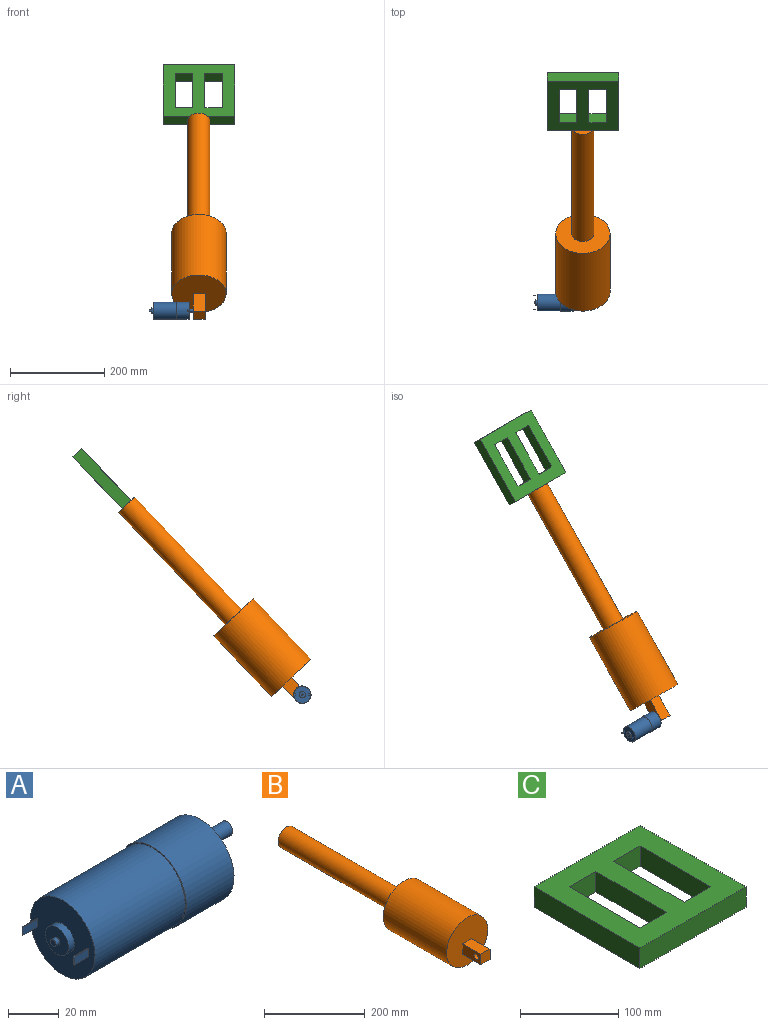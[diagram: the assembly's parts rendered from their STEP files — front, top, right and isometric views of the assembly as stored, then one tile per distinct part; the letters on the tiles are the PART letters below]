
ASSEMBLY  parts=3 mates=5
PART A: 70 faces, bbox 106.2x37x37 mm
  f0: torus R=1.65mm, axis (1,0,0), area 2.2mm2, adj f5,f45
  f1: torus R=1.65mm, axis (1,0,0), area 2.2mm2, adj f3,f47
  f2: torus R=1.65mm, axis (1,0,0), area 2.2mm2, adj f4,f46
  f3: cylinder r=1.78mm len=3.56mm, axis (-1,0,0), area 24.1mm2, adj f1,f19
  f4: cylinder r=1.78mm len=3.56mm, axis (-1,0,0), area 24.1mm2, adj f2,f20
  f5: cylinder r=1.78mm len=3.56mm, axis (-1,0,0), area 24.1mm2, adj f0,f21
  f6: cylinder r=1.91mm len=3.81mm, axis (1,0,0), area 30.4mm2, adj f20,f25
  f7: cylinder r=1.91mm len=3.81mm, axis (1,0,0), area 30.4mm2, adj f21,f25
  f8: cylinder r=1.91mm len=3.81mm, axis (1,0,0), area 30.4mm2, adj f19,f25
  f9: cylinder r=1.57mm len=3.15mm, axis (1,0,0), area 21.1mm2, adj f23,f32
  f10: cylinder r=6.45mm len=12.9mm, axis (1,0,0), area 128.7mm2, adj f22,f23
  f11: cylinder r=1.73mm len=3.5mm, axis (1,0,0), area 38mm2, adj f25,f31
  f12: cylinder r=1.73mm len=3.5mm, axis (1,0,0), area 38mm2, adj f25,f30
  f13: cylinder r=1.73mm len=3.5mm, axis (1,0,0), area 38mm2, adj f25,f29
  f14: cylinder r=1.73mm len=3.5mm, axis (1,0,0), area 38mm2, adj f25,f28
  f15: cylinder r=3.17mm len=20.2mm, axis (-1,0,0), area 334.8mm2, adj f24,f27,f43,f44,f69
  f16: cylinder r=6mm len=12mm, axis (-1,0,0), area 50.9mm2, adj f24,f25
  f17: cylinder r=18.5mm len=37mm, axis (-1,0,0), area 3080.9mm2, adj f25,f26
  f18: cylinder r=17.9mm len=50mm, axis (1,0,0), area 5623.5mm2, adj f22,f26
  f19: plane 3.81x3.81mm, normal (1,0,0), area 1.5mm2, adj f3,f8
  f20: plane 3.81x3.81mm, normal (1,0,0), area 1.5mm2, adj f4,f6
  f21: plane 3.81x3.81mm, normal (1,0,0), area 1.5mm2, adj f5,f7
  f22: plane 35.8x35.8mm, normal (-1,0,0), area 872.1mm2, adj f10,f18,f33,f34,f35,f36,f38,f39
  f23: plane 12.9x12.9mm, normal (-1,0,0), area 123mm2, adj f9,f10
  f24: plane 12x12mm, normal (1,0,0), area 81.4mm2, adj f15,f16
  f25: plane 37x37mm, normal (1,0,0), area 890.4mm2, adj f6,f7,f8,f11,f12,f13,f14,f16
  f26: plane 37x37mm, normal (-1,0,0), area 68.6mm2, adj f17,f18
  f27: plane 4.51x0.94mm, normal (1,0,0), area 2.9mm2, adj f15,f69
  f28: plane 3.45x3.45mm, normal (1,0,0), area 9.4mm2, adj f14
  f29: plane 3.45x3.45mm, normal (1,0,0), area 9.4mm2, adj f13
  f30: plane 3.45x3.45mm, normal (1,0,0), area 9.4mm2, adj f12
  f31: plane 3.45x3.45mm, normal (1,0,0), area 9.4mm2, adj f11
  f32: plane 3.15x3.15mm, normal (-1,0,0), area 7.8mm2, adj f9
  f33: plane 8.13x0.48mm, normal (0,0,1), area 3.9mm2, adj f22,f34,f36,f37
  f34: plane 8.13x3.86mm, normal (0,1,0), area 31.4mm2, adj f22,f33,f35,f37
  f35: plane 8.13x0.48mm, normal (0,0,-1), area 3.9mm2, adj f22,f34,f36,f37
  f36: plane 8.13x3.86mm, normal (0,-1,0), area 31.4mm2, adj f22,f33,f35,f37
  f37: plane 3.86x0.48mm, normal (-1,0,0), area 1.9mm2, adj f33,f34,f35,f36
  f38: plane 8.13x0.48mm, normal (0,0,1), area 3.9mm2, adj f22,f39,f41,f42
  f39: plane 8.13x3.86mm, normal (0,1,0), area 31.4mm2, adj f22,f38,f40,f42
  f40: plane 8.13x0.48mm, normal (0,0,-1), area 3.9mm2, adj f22,f39,f41,f42
  f41: plane 8.13x3.86mm, normal (0,-1,0), area 31.4mm2, adj f22,f38,f40,f42
  f42: plane 3.86x0.48mm, normal (-1,0,0), area 1.9mm2, adj f38,f39,f40,f41
  f43: plane 11.75x4.96mm, normal (0,1,0), area 58.3mm2, adj f15,f44,f69
  f44: plane 6.35x5.16mm, normal (1,0,0), area 27.5mm2, adj f15,f43
  f45: plane 3.3x3.3mm, normal (1,0,0), area 3.7mm2, adj f0,f48,f49,f50,f51,f52,f53
  f46: plane 3.3x3.3mm, normal (1,0,0), area 3.7mm2, adj f2,f55,f56,f57,f58,f59,f60
  f47: plane 3.3x3.3mm, normal (1,0,0), area 3.7mm2, adj f1,f62,f63,f64,f65,f66,f67
  f48: plane 1.38x1.27mm, normal (0,1,0), area 1.7mm2, adj f45,f49,f53,f54
  f49: plane 1.27x1.19mm, normal (0,0.5,-0.87), area 1.7mm2, adj f45,f48,f50,f54
  f50: plane 1.27x1.19mm, normal (0,-0.5,-0.87), area 1.7mm2, adj f45,f49,f51,f54
  f51: plane 1.38x1.27mm, normal (0,-1,0), area 1.7mm2, adj f45,f50,f52,f54
  f52: plane 1.27x1.19mm, normal (0,-0.5,0.87), area 1.7mm2, adj f45,f51,f53,f54
  f53: plane 1.27x1.19mm, normal (0,0.5,0.87), area 1.7mm2, adj f45,f48,f52,f54
  f54: plane 2.75x2.38mm, normal (1,0,0), area 4.9mm2, adj f48,f49,f50,f51,f52,f53
  f55: plane 1.27x1.19mm, normal (0,0.5,-0.87), area 1.7mm2, adj f46,f56,f60,f61
  f56: plane 1.27x1.19mm, normal (0,-0.5,-0.87), area 1.7mm2, adj f46,f55,f57,f61
  f57: plane 1.38x1.27mm, normal (0,-1,0), area 1.7mm2, adj f46,f56,f58,f61
  f58: plane 1.27x1.19mm, normal (0,-0.5,0.87), area 1.7mm2, adj f46,f57,f59,f61
  f59: plane 1.27x1.19mm, normal (0,0.5,0.87), area 1.7mm2, adj f46,f58,f60,f61
  f60: plane 1.38x1.27mm, normal (0,1,0), area 1.7mm2, adj f46,f55,f59,f61
  f61: plane 2.75x2.38mm, normal (1,0,0), area 4.9mm2, adj f55,f56,f57,f58,f59,f60
  f62: plane 1.38x1.27mm, normal (0,1,0), area 1.7mm2, adj f47,f63,f67,f68
  f63: plane 1.27x1.19mm, normal (0,0.5,-0.87), area 1.7mm2, adj f47,f62,f64,f68
  f64: plane 1.27x1.19mm, normal (0,-0.5,-0.87), area 1.7mm2, adj f47,f63,f65,f68
  f65: plane 1.38x1.27mm, normal (0,-1,0), area 1.7mm2, adj f47,f64,f66,f68
  f66: plane 1.27x1.19mm, normal (0,-0.5,0.87), area 1.7mm2, adj f47,f65,f67,f68
  f67: plane 1.27x1.19mm, normal (0,0.5,0.87), area 1.7mm2, adj f47,f62,f66,f68
  f68: plane 2.75x2.38mm, normal (1,0,0), area 4.9mm2, adj f62,f63,f64,f65,f66,f67
  f69: cylinder r=0.25mm len=4.96mm, axis (0,0,1), area 1.9mm2, adj f15,f27,f43
PART B: 12 faces, bbox 115.7x558.8x115.7 mm
  f0: plane 115.65x115.65mm, normal (0,-1,0), area 9860mm2, adj f1,f5,f6,f7,f8
  f1: cylinder r=57.83mm len=177.8mm, axis (0,1,0), area 64600.8mm2, adj f0,f2
  f2: plane 115.65x115.65mm, normal (0,1,0), area 8764.5mm2, adj f1,f3
  f3: cylinder r=23.54mm len=330.2mm, axis (0,-1,0), area 48836.1mm2, adj f2,f4
  f4: plane 47.08x47.08mm, normal (0,1,0), area 1740.7mm2, adj f3
  f5: plane 50.8x25.4mm, normal (0,0,-1), area 1290.3mm2, adj f0,f6,f8,f9
  f6: plane 50.8x25.4mm, normal (1,0,0), area 1290.3mm2, adj f0,f5,f7,f9
  f7: plane 50.8x25.4mm, normal (0,0,1), area 1290.3mm2, adj f0,f6,f8,f9
  f8: plane 50.8x25.4mm, normal (-1,0,0), area 1163.6mm2, adj f0,f5,f7,f9,f10
  f9: plane 25.4x25.4mm, normal (0,-1,0), area 645.2mm2, adj f5,f6,f7,f8
  f10: cylinder r=6.35mm len=12.7mm, axis (-1,0,0), area 506.7mm2, adj f8,f11
  f11: plane 12.7x12.7mm, normal (-1,0,0), area 126.7mm2, adj f10
PART C: 14 faces, bbox 152.4x152.4x25.4 mm
  f0: plane 38.1x25.4mm, normal (0,1,0), area 967.7mm2, adj f5,f6,f8,f9
  f1: plane 38.1x25.4mm, normal (0,1,0), area 967.7mm2, adj f5,f6,f7,f10
  f2: plane 152.4x25.4mm, normal (-1,0,0), area 3871mm2, adj f3,f5,f6,f12
  f3: plane 152.4x25.4mm, normal (0,-1,0), area 3871mm2, adj f2,f4,f5,f6
  f4: plane 152.4x25.4mm, normal (1,0,0), area 3871mm2, adj f3,f5,f6,f12
  f5: plane 152.4x152.4mm, normal (0,0,1), area 15483.8mm2, adj f0,f1,f2,f3,f4,f7,f8,f9
  f6: plane 152.4x152.4mm, normal (0,0,-1), area 15483.8mm2, adj f0,f1,f2,f3,f4,f7,f8,f9
  f7: plane 101.6x25.4mm, normal (-1,0,0), area 2580.6mm2, adj f1,f5,f6,f11
  f8: plane 101.6x25.4mm, normal (1,0,0), area 2580.6mm2, adj f0,f5,f6,f13
  f9: plane 101.6x25.4mm, normal (-1,0,0), area 2580.6mm2, adj f0,f5,f6,f13
  f10: plane 101.6x25.4mm, normal (1,0,0), area 2580.6mm2, adj f1,f5,f6,f11
  f11: plane 38.1x25.4mm, normal (0,-1,0), area 967.7mm2, adj f5,f6,f7,f10
  f12: plane 152.4x25.4mm, normal (0,1,0), area 3871mm2, adj f2,f4,f5,f6
  f13: plane 38.1x25.4mm, normal (0,-1,0), area 967.7mm2, adj f5,f6,f8,f9
PLACE A t=(-120.24,-93.53,149.94)mm fixed
PLACE B rot(axis=(1,0,0),46.4deg) t=(-72.84,52.6,314.69)mm
PLACE C rot(axis=(1,0,0),46.4deg) t=(-149.04,306.83,563.65)mm
MATE cylindrical A.f15 <-> B.f10  axis (-1,0,0) through (-82.29,-86.53,149.94)mm
MATE planar C.f3 <-> B.f3  axis (0,-0.69,-0.72) through (-72.84,280.13,553.99)mm
MATE parallel C.f3 <-> B.f3  axis (0,-0.69,-0.72) through (-72.84,280.13,553.99)mm
MATE planar A.f44 <-> B.f10  axis (1,0,0) through (-72.18,-86.9,149.94)mm
MATE fastened B.f3 <-> C.f3  axis (0,0.69,0.72) through (-72.84,280.13,553.99)mm
